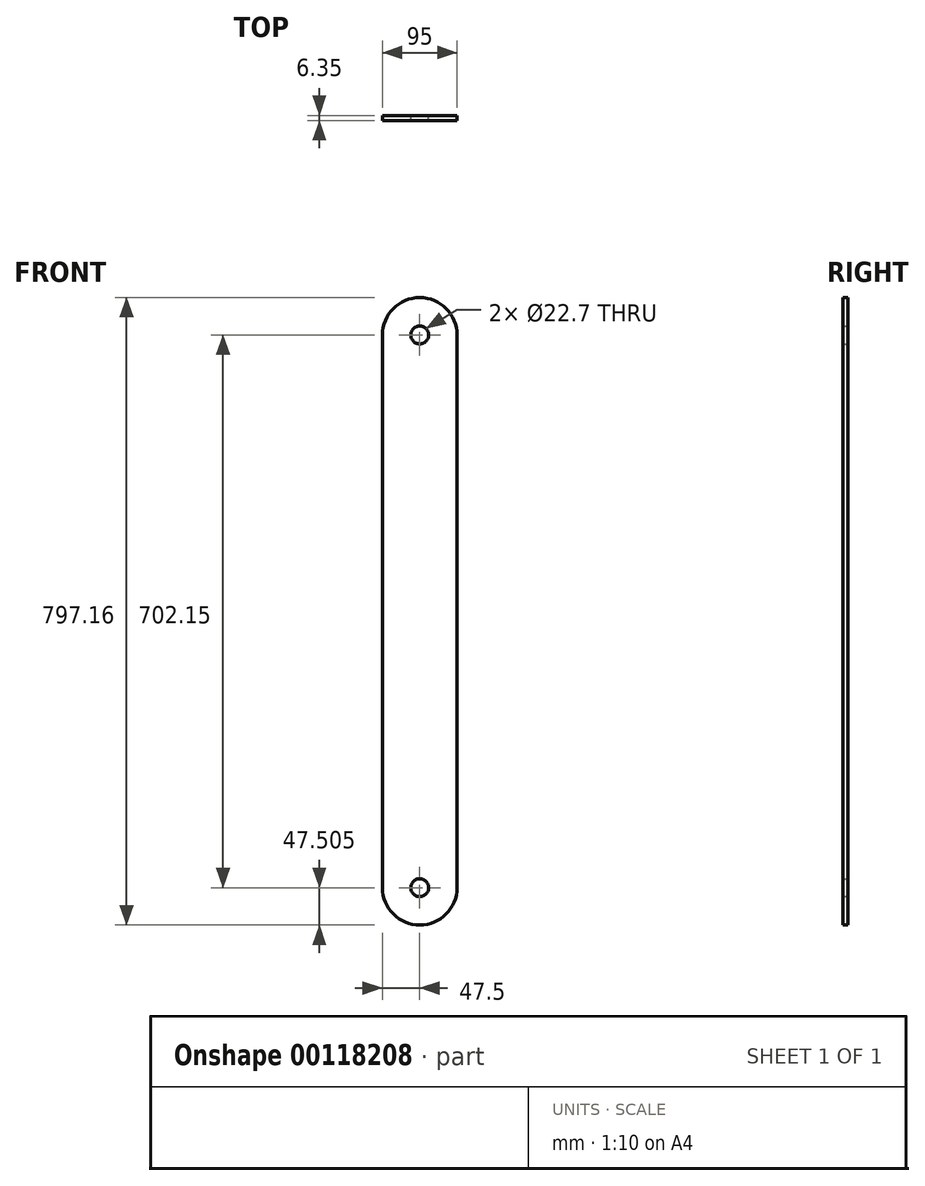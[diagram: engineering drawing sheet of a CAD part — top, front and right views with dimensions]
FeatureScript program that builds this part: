
annotation { "Feature Type Name" : "Feature", "Feature Type Description" : "" }
export const myFeature = defineFeature(function(context is Context, id is Id, definition is map)
    precondition{}
    {
        {
            var Q0;
            Q0=qCreatedBy(makeId("Front.planeOp"),FACE);
            var sketch = newSketch(context, id + "F0", { "sketchPlane" : qUnion([Q0])});
            skArc(sketch, "E0", {"start": v(47.5, 351.07) * mm, "mid": v(0, 398.57) * mm, "end": v(-47.5, 351.07) * mm});
            skLineSegment(sketch, "E1", {"start": v(47.5, 351.07) * mm, "end": v(47.5, -351.07) * mm});
            skArc(sketch, "E2", {"start": v(-47.5, -351.07) * mm, "mid": v(0, -398.57) * mm, "end": v(47.5, -351.07) * mm});
            skLineSegment(sketch, "E3", {"start": v(-47.5, 351.08) * mm, "end": v(-47.5, -351.07) * mm});
            skCircle(sketch, "E4", {"center": v(0, 351.07) * mm, "radius": 11.35 * mm});
            skCircle(sketch, "E5", {"center": v(0, -351.07) * mm, "radius": 11.35 * mm});
            skLineSegment(sketch, "E6", {"start": v(-104.82, -398.57) * mm, "end": v(199.23, -398.57) * mm, "construction": true});
            skLineSegment(sketch, "E7", {"start": v(-74.18, 398.57) * mm, "end": v(110.84, 398.57) * mm, "construction": true});
            skSolve(sketch);
        }
        {
            var Q0;
            Q0 = qSketchRegion(id + "F0", true);
            extrude(context, id + "F1", {"entities" : qUnion([Q0]), "depth" : 6.35 * mm});
        }
    });
